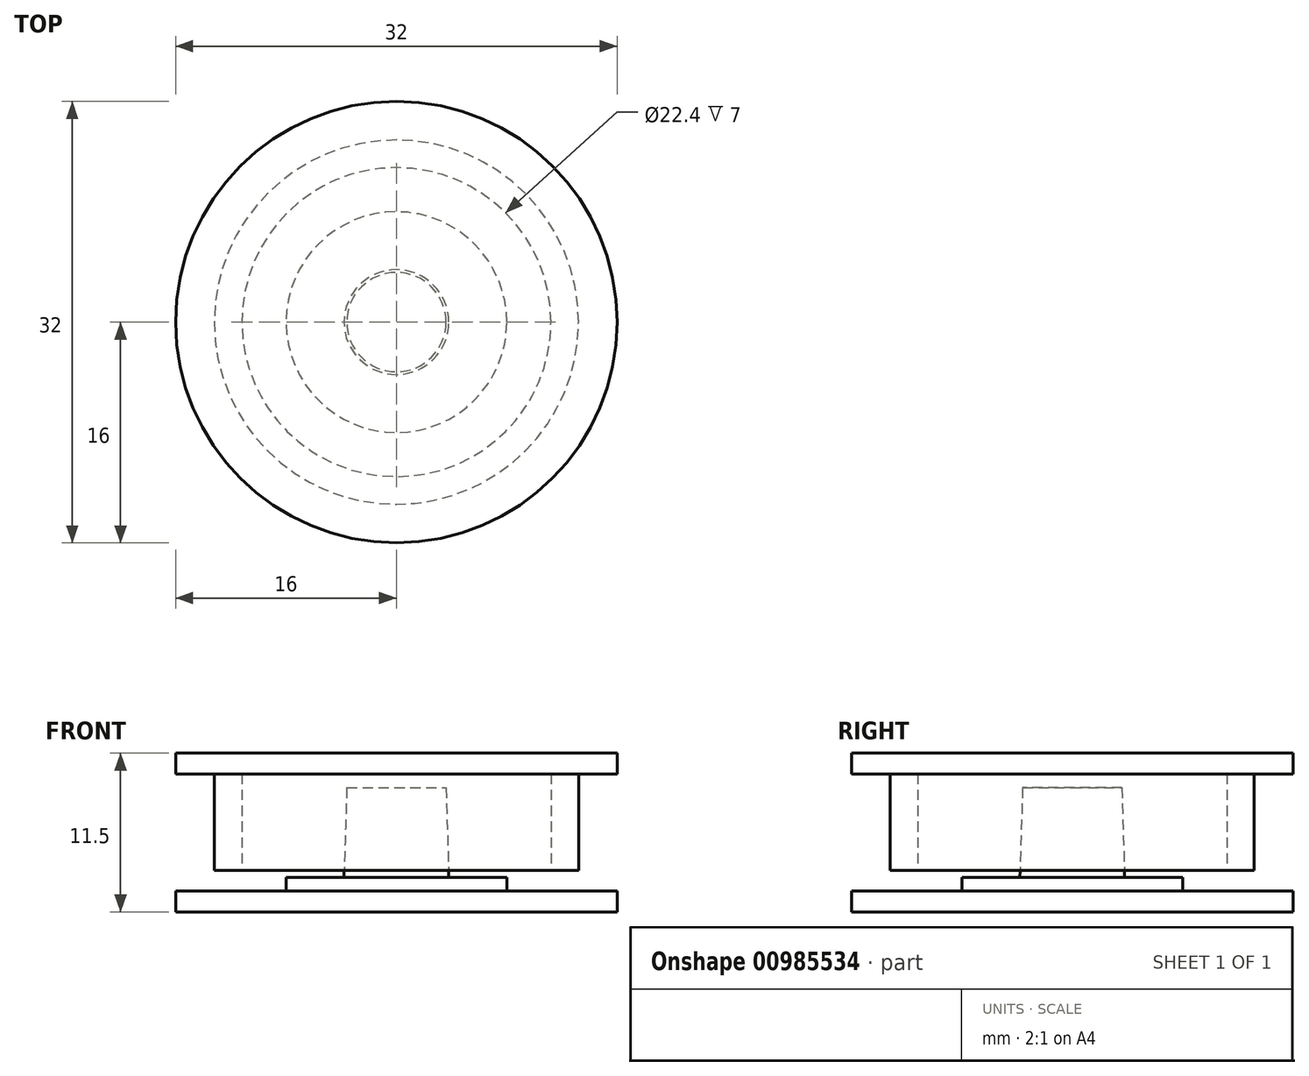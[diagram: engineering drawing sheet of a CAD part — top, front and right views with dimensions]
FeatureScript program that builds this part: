
annotation { "Feature Type Name" : "Feature", "Feature Type Description" : "" }
export const myFeature = defineFeature(function(context is Context, id is Id, definition is map)
    precondition{}
    {
        {
            var Q0;
            Q0=qCreatedBy(makeId("Front.planeOp"),FACE);
            var sketch = newSketch(context, id + "F0", { "sketchPlane" : qUnion([Q0])});
            skLineSegment(sketch, "E0", {"start": v(0, 0) * mm, "end": v(0, 9) * mm});
            skLineSegment(sketch, "E1", {"start": v(0, 9) * mm, "end": v(3.6, 9) * mm});
            skLineSegment(sketch, "E2", {"start": v(3.6, 9) * mm, "end": v(3.8, 2.5) * mm});
            skLineSegment(sketch, "E3", {"start": v(3.8, 2.5) * mm, "end": v(8, 2.5) * mm});
            skLineSegment(sketch, "E4", {"start": v(8, 2.5) * mm, "end": v(8, 1.5) * mm});
            skLineSegment(sketch, "E5", {"start": v(8, 1.5) * mm, "end": v(16, 1.5) * mm});
            skLineSegment(sketch, "E6", {"start": v(16, 1.5) * mm, "end": v(16, 0) * mm});
            skLineSegment(sketch, "E7", {"start": v(16, 0) * mm, "end": v(0, 0) * mm});
            skSolve(sketch);
        }
        {
            var Q0;
            Q0 = qSketchRegion(id + "F0", true);
            var Q1;
            Q1=sQuery(id+"F0.wireOp",EDGE,"E0");
            revolve(context, id + "F1", {"surfaceOperationType" : NewSurfaceOperationType.NEW, "entities" : qUnion([Q0]), "axis" : qUnion([Q1]), "revolveType" : RevolveType.FULL});
        }
        {
            var Q0;
            Q0=qCreatedBy(makeId("Front.planeOp"),FACE);
            var sketch = newSketch(context, id + "F2", { "sketchPlane" : qUnion([Q0])});
            skLineSegment(sketch, "E8", {"start": v(0, 10) * mm, "end": v(0, 11.5) * mm});
            skLineSegment(sketch, "E9", {"start": v(0, 11.5) * mm, "end": v(16, 11.5) * mm});
            skLineSegment(sketch, "E10", {"start": v(16, 11.5) * mm, "end": v(16, 10) * mm});
            skLineSegment(sketch, "E11", {"start": v(16, 10) * mm, "end": v(13.2, 10) * mm});
            skLineSegment(sketch, "E12", {"start": v(13.2, 10) * mm, "end": v(13.2, 3) * mm});
            skLineSegment(sketch, "E13", {"start": v(13.2, 3) * mm, "end": v(11.2, 3) * mm});
            skLineSegment(sketch, "E14", {"start": v(11.2, 3) * mm, "end": v(11.2, 10) * mm});
            skLineSegment(sketch, "E15", {"start": v(11.2, 10) * mm, "end": v(0, 10) * mm});
            skSolve(sketch);
        }
        {
            var Q0;
            Q0 = qSketchRegion(id + "F2", true);
            var Q1;
            Q1=sQuery(id+"F2.wireOp",EDGE,"E8");
            revolve(context, id + "F3", {"surfaceOperationType" : NewSurfaceOperationType.NEW, "entities" : qUnion([Q0]), "axis" : qUnion([Q1]), "revolveType" : RevolveType.FULL});
        }
    });
